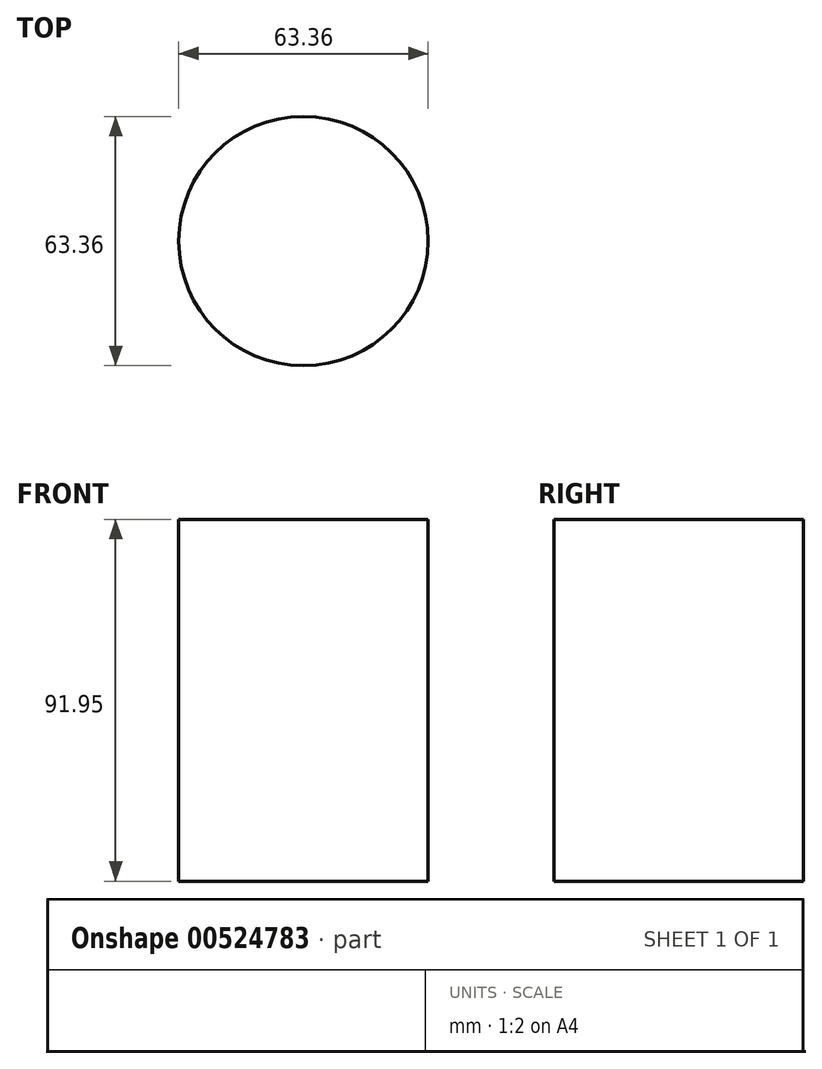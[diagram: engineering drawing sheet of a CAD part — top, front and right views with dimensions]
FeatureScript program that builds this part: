
annotation { "Feature Type Name" : "Feature", "Feature Type Description" : "" }
export const myFeature = defineFeature(function(context is Context, id is Id, definition is map)
    precondition{}
    {
        {
            var Q0;
            Q0=qCreatedBy(makeId("Top.planeOp"),FACE);
            var sketch = newSketch(context, id + "F0", { "sketchPlane" : qUnion([Q0])});
            skCircle(sketch, "E0", {"center": v(0, 0) * mm, "radius": 31.68 * mm});
            skSolve(sketch);
        }
        {
            var Q0;
            Q0 = qSketchRegion(id + "F0", true);
            extrude(context, id + "F1", {"entities" : qUnion([Q0]), "depth" : 91.95 * mm, "offsetDistance" : 25.4 * mm});
        }
    });
